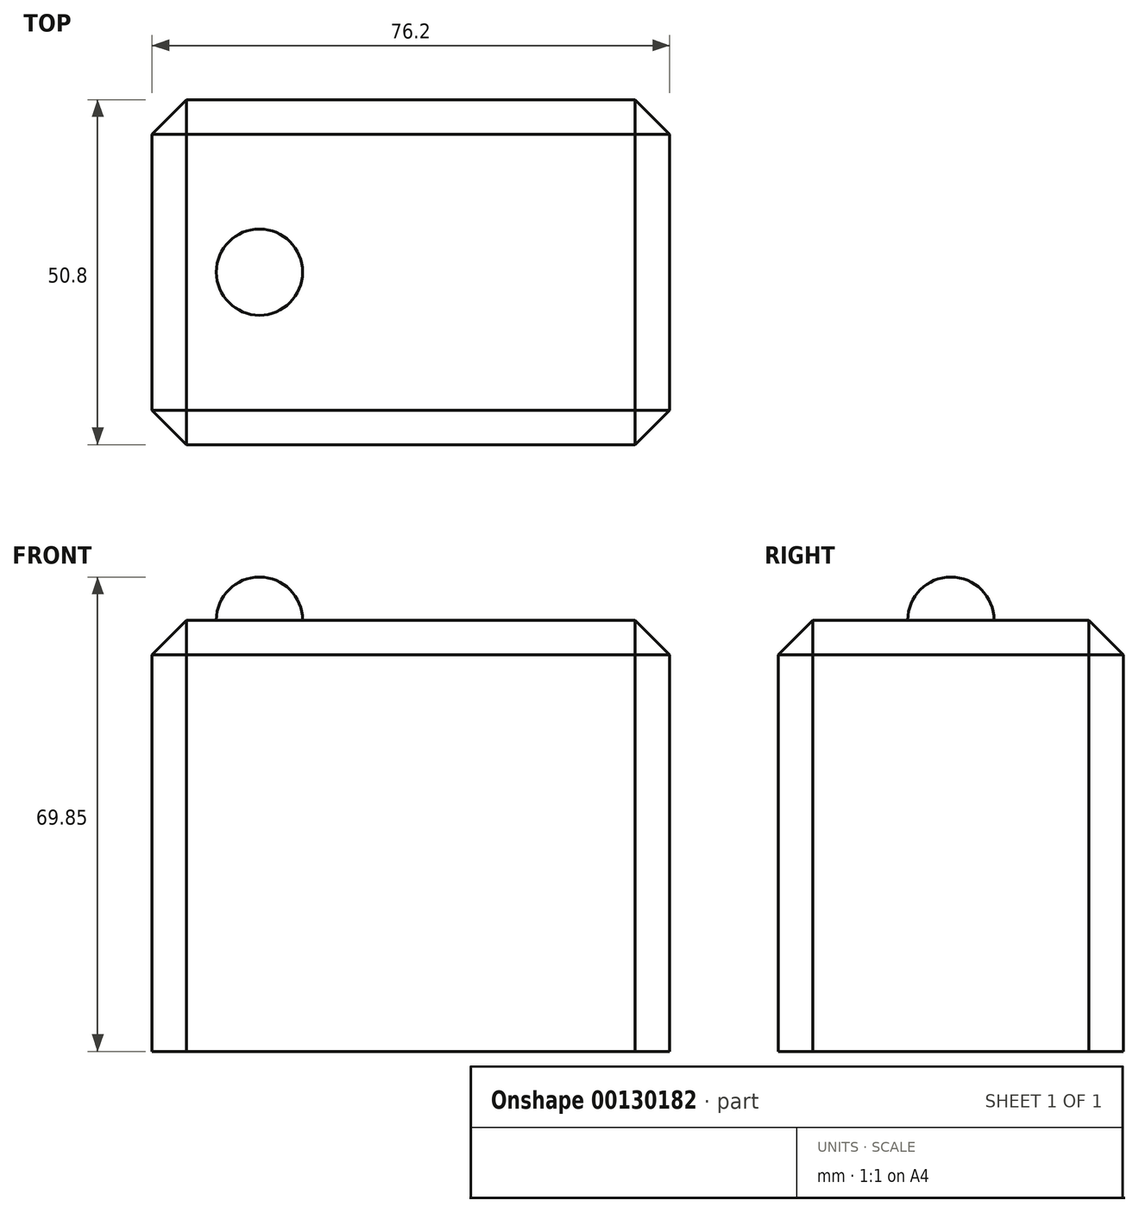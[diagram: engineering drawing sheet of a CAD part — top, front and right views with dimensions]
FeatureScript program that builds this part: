
annotation { "Feature Type Name" : "Feature", "Feature Type Description" : "" }
export const myFeature = defineFeature(function(context is Context, id is Id, definition is map)
    precondition{}
    {
        {
            var Q0;
            Q0=qCreatedBy(makeId("Top.planeOp"),FACE);
            var sketch = newSketch(context, id + "F0", { "sketchPlane" : qUnion([Q0])});
            skLineSegment(sketch, "E0.bottom", {"start": v(-32.05, 20.5) * mm, "end": v(44.15, 20.5) * mm});
            skLineSegment(sketch, "E0.top", {"start": v(-32.05, -30.3) * mm, "end": v(44.15, -30.3) * mm});
            skLineSegment(sketch, "E0.left", {"start": v(-32.05, 20.5) * mm, "end": v(-32.05, -30.3) * mm});
            skLineSegment(sketch, "E0.right", {"start": v(44.15, 20.5) * mm, "end": v(44.15, -30.3) * mm});
            skSolve(sketch);
        }
        {
            var Q0;
            Q0 = qSketchRegion(id + "F0", true);
            extrude(context, id + "F1", {"entities" : qUnion([Q0]), "depth" : 63.5 * mm});
        }
        {
            var Q0;
            Q0=makeQuery(id+"F1.opExtrude","SWEPT_EDGE",EDGE,{"disambiguationData":[OSD([sQuery(id+"F0.wireOp",EDGE,"E0.bottom"),sQuery(id+"F0.wireOp",EDGE,"E0.left")])]});
            var Q1;
            Q1=makeQuery(id+"F1.opExtrude","CAP_EDGE",EDGE,{"disambiguationData":[OSD([sQuery(id+"F0.wireOp",EDGE,"E0.bottom")])],"isStart":false});
            var Q2;
            Q2=makeQuery(id+"F1.opExtrude","CAP_EDGE",EDGE,{"disambiguationData":[OSD([sQuery(id+"F0.wireOp",EDGE,"E0.left")])],"isStart":false});
            var Q3;
            Q3=makeQuery(id+"F1.opExtrude","SWEPT_EDGE",EDGE,{"disambiguationData":[OSD([sQuery(id+"F0.wireOp",EDGE,"E0.top"),sQuery(id+"F0.wireOp",EDGE,"E0.left")])]});
            var Q4;
            Q4=makeQuery(id+"F1.opExtrude","CAP_EDGE",EDGE,{"disambiguationData":[OSD([sQuery(id+"F0.wireOp",EDGE,"E0.right")])],"isStart":false});
            var Q5;
            Q5=makeQuery(id+"F1.opExtrude","SWEPT_EDGE",EDGE,{"disambiguationData":[OSD([sQuery(id+"F0.wireOp",EDGE,"E0.bottom"),sQuery(id+"F0.wireOp",EDGE,"E0.right")])]});
            var Q6;
            Q6=makeQuery(id+"F1.opExtrude","SWEPT_EDGE",EDGE,{"disambiguationData":[OSD([sQuery(id+"F0.wireOp",EDGE,"E0.top"),sQuery(id+"F0.wireOp",EDGE,"E0.right")])]});
            var Q7;
            Q7=makeQuery(id+"F1.opExtrude","CAP_EDGE",EDGE,{"disambiguationData":[OSD([sQuery(id+"F0.wireOp",EDGE,"E0.top")])],"isStart":false});
            chamfer(context, id + "F2", {"entities" : qUnion([Q0, Q1, Q2, Q3, Q4, Q5, Q6, Q7]), "width" : 5.08 * mm, "tangentPropagation" : true});
        }
        {
            var Q0;
            Q0=makeQuery(id+"F1.opExtrude","CAP_FACE",FACE,{"disambiguationData":[OSD([sQuery(id+"F0.wireOp",EDGE,"E0.bottom"),sQuery(id+"F0.wireOp",EDGE,"E0.top"),sQuery(id+"F0.wireOp",EDGE,"E0.left"),sQuery(id+"F0.wireOp",EDGE,"E0.right")])],"isStart":false});
            var sketch = newSketch(context, id + "F3", { "sketchPlane" : qUnion([Q0])});
            skPoint(sketch, "E1.centerSnap0", {"position": v(-26.97, -4.9) * mm});
            skArc(sketch, "E2", {"start": v(-16.24, -11.24) * mm, "mid": v(-9.89, -4.9) * mm, "end": v(-16.24, 1.46) * mm});
            skLineSegment(sketch, "E3", {"start": v(-16.24, -4.9) * mm, "end": v(-16.24, 1.46) * mm});
            skLineSegment(sketch, "E4", {"start": v(-16.24, 1.46) * mm, "end": v(-16.24, -11.24) * mm});
            skSolve(sketch);
        }
        {
            var Q0;
            {var subQ0=sQuery(id+"F3.wireOp",EDGE,"E2");Q0=makeQuery(id+"F3.imprint","IMPRINT",FACE,{"disambiguationData":[TD([[makeQuery(id+"F3.imprint","IMPRINT",EDGE,{"derivedFrom":subQ0}),1.0]])]});}
            var Q1;
            Q1=sQuery(id+"F3.wireOp",EDGE,"E4");
            revolve(context, id + "F4", {"operationType" : NewBodyOperationType.ADD, "entities" : qUnion([Q0]), "axis" : qUnion([Q1]), "revolveType" : RevolveType.FULL});
        }
    });
